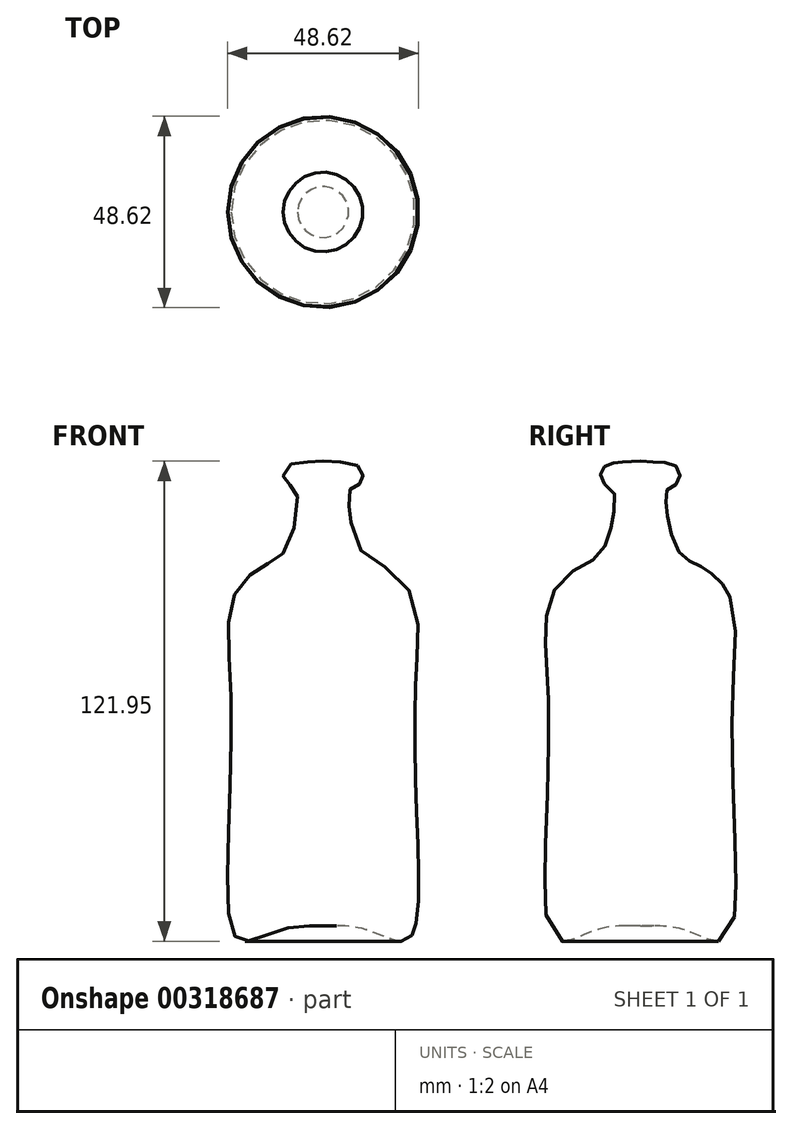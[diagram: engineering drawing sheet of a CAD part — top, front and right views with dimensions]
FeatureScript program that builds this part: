
annotation { "Feature Type Name" : "Feature", "Feature Type Description" : "" }
export const myFeature = defineFeature(function(context is Context, id is Id, definition is map)
    precondition{}
    {
        {
            var Q0;
            Q0=qCreatedBy(makeId("Front.planeOp"),FACE);
            var sketch = newSketch(context, id + "F0", { "sketchPlane" : qUnion([Q0])});
            skFitSpline(sketch, "E0", {"points": [v(0, -60.85) * mm, v(-9.82, -61.45) * mm, v(-18.15, -64.42) * mm, v(-22.32, -63.53) * mm, v(-24.1, -40.62) * mm, v(-23.5, 0) * mm, v(-22.61, 23.06) * mm, v(-14.88, 30.8) * mm, v(-9.22, 35.26) * mm, v(-7.14, 50.73) * mm, v(-9.52, 51.63) * mm, v(-9.52, 55.5) * mm, v(-5.06, 56.98) * mm, v(0, 57.28) * mm], "startDerivative": vector(-133.64, 4.3) * mm, "endDerivative": vector(91.68, 5.25) * mm});
            skLineSegment(sketch, "E1", {"start": v(0, 57.28) * mm, "end": v(0, -60.85) * mm});
            skSolve(sketch);
        }
        {
            var Q0;
            Q0=qCreatedBy(makeId("Front.planeOp"),FACE);
            var sketch = newSketch(context, id + "F1", { "sketchPlane" : qUnion([Q0])});
            skLineSegment(sketch, "E2", {"start": v(0, -76.62) * mm, "end": v(0, 76.62) * mm, "construction": true});
            skSolve(sketch);
        }
        {
            var Q0;
            Q0=makeQuery(id+"F0.imprint","IMPRINT",FACE,{"disambiguationData":[TD([[makeQuery(id+"F0.imprint","IMPRINT",EDGE,{"derivedFrom":sQuery(id+"F0.wireOp",EDGE,"E0")}),-1.0]])]});
            var Q1;
            Q1=sQuery(id+"F1.wireOp",EDGE,"E2");
            revolve(context, id + "F2", {"entities" : qUnion([Q0]), "axis" : qUnion([Q1]), "revolveType" : RevolveType.FULL});
        }
    });
